# Revit family: PRD_FrankeWS_Snks_WorkroomSink_SIRW774
name_source: partatom
category: Plumbing Fixtures
revit_build: Autodesk Revit 2018 (Build: 20190510_1515(x64)
units: mm (PartAtom-declared; Revit-internal decimal feet)

## family parameters
Cut with Voids When Loaded = Yes
Host = Face
OmniClass Number = 23.45.05.14.14.17
OmniClass Title = Plaster Sinks
Part Type = Normal
Room Calculation Point = No
Round Connector Dimension = Use Diameter
Shared = Yes

## types (1)
- SIRW774
    AssetType = Fixed
    BIMObjectName = PRD_AR_Sinks_WorkroomSink_SIRW774
    BowlDepth = 560.00 mm
    BowlFinish = High polished
    BowlHeight = 283.00 mm
    BowlPosition = Center
    BowlWidth = 1960.00 mm
    Brushes = Without brushes
    Category = Pr_40_20_96_81, Sinks
    Color = Alpine white
    Default Elevation = 0 mm  [stored 0 ft]
    Description = Workroom sink made of MIRANIT resin-bonded mineral material with pore-free smooth surface (temperature-resistant up to 80 °C). Basin without tap landing. Large inner radii, bottom of basin with 2° slope. Alpine white colour. Welded substructure frame, powder-coated in basin colour, adjustable base feet. Mounting material included. Stand pipe valve DN 40 x 200 mm and protective strainer (removable) made of stainless steel.
    DiameterNominal = 40  [stored 0.131234 ft]
    DrainSize = 40 mm  [stored 0.131234 ft]
    DrainerOrStorage = No
    DurationUnit = year
    Features = resin-bonded mineral material with pore-free smooth surface
    Finish = Coated
    Grid = No
    GrossWeight = 160.00 kg
    IfcExportAs = IfcSanitaryTerminalType
    IfcExportType = SINK
    IntegralAccessories = incl. mounting material
    Manufacturer = KWC Group AG
    ManufacturerName = KWC Group AG
    ManufacturerURL = www.kwc.com
    Material = mineral material
    MaterialCode = Miranit
    Model = SIRW774
    ModelNumber = 2000102724
    ModelReference = SIRW774
    Mounting = Pedestal
    MountingOffset = 0 mm  [stored 0 ft]
    NBSDescription = Sinks
    NBSReference = 45-35-70/344
    Name = Workroom Sink SIRW774
    NetWeight = 152.00 kg
    NominalDepth = 600 mm
    NominalHeight = 800 mm  [stored 2.62467 ft]
    NominalWidth = 2000 mm  [stored 6.56168 ft]
    NumberOfWasteHoles = 1
    OutletSize = DN 40
    Overflow = Standpipe overflow
    ProductInformation = https://pim.kwc.com
    RearUpstand = No
    Shape = Cuboid
    SinkMaterial = PRD_AR_ResinBondedMaterial_White
    SinkType = Plaster
    Size = 2000 x 300/800 x 600 mm (W x H x D)
    Spillway = No
    Splashback = No
    StandMaterial = PRD_AR_Black
    StrainerMaterial = PRD_AR_StainlessSteel_SatinFinished
    Sump = No
    SumpBasket = No
    TapLedge = No
    TypeOfMounting = Wall and floor mounting
    TypeOfUtilitySink = Cleaner sink
    TypeOfWasteKit = Standpipe strainer
    URL = www.kwc.com
    Uniclass2015Code = Pr_40_20_96_81
    Uniclass2015Title = Sinks
    Uniclass2015Version = Products v1.17
    UpperEdgeOfBasinHeight = 800.00 mm
    Version = 1
    WarrantyDurationUnit = year
    WashRiffle = No
    WasteHolePosition = Center back
    WasteHoleProjection = 145.00 mm
    WasteKitIncluded = Yes
    WasteSize = DN 40

note: [stored X ft] marks values corroborated as IEEE doubles in the binary element streams (Revit-internal decimal feet)

## geometry (parser evidence)
native form markers: Sweep x5
no freeform markers — native parametric forms only
